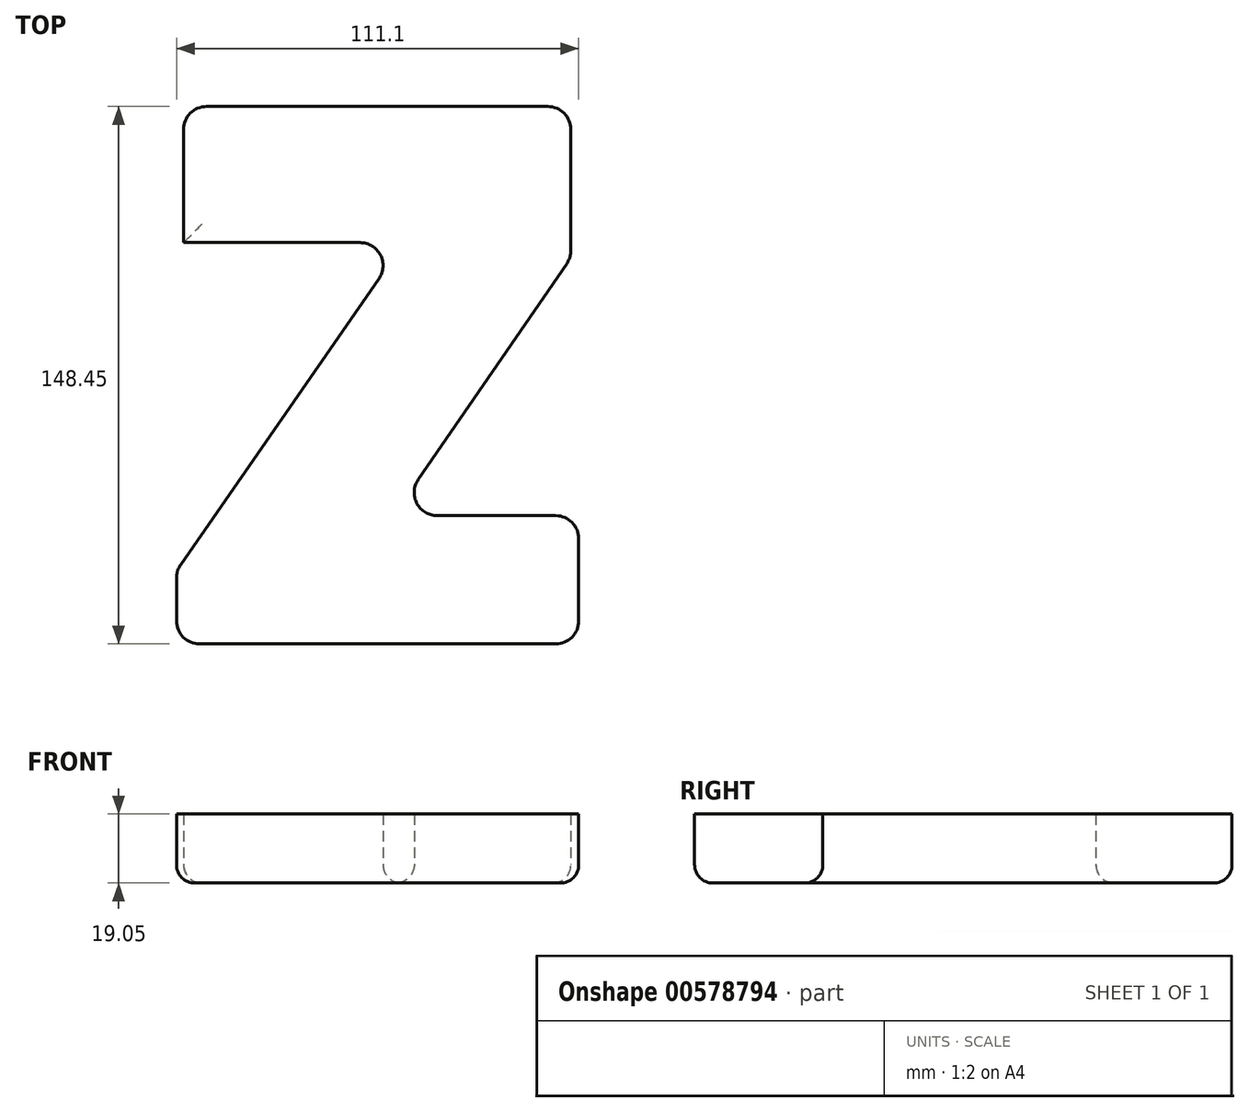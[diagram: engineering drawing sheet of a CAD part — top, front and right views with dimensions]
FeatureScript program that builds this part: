
annotation { "Feature Type Name" : "Feature", "Feature Type Description" : "" }
export const myFeature = defineFeature(function(context is Context, id is Id, definition is map)
    precondition{}
    {
        {
            var Q0;
            Q0=qCreatedBy(makeId("Top.planeOp"),FACE);
            var sketch = newSketch(context, id + "F0", { "sketchPlane" : qUnion([Q0])});
            skText(sketch, "E0", { "text": "Z", "fontName": "OpenSans-Bold.ttf"});
            skLineSegment(sketch, "E1", {"start": v(-54.55, 77.63) * mm, "end": v(-54.55, 38.1) * mm});
            skLineSegment(sketch, "E2", {"start": v(-54.55, 38.1) * mm, "end": v(-5.8, 38.1) * mm});
            skLineSegment(sketch, "E3", {"start": v(-0.58, 28.14) * mm, "end": v(-55.35, -50.87) * mm});
            skLineSegment(sketch, "E4", {"start": v(-56.48, -54.49) * mm, "end": v(-56.48, -66.4) * mm});
            skLineSegment(sketch, "E5", {"start": v(-50.13, -72.75) * mm, "end": v(48.27, -72.75) * mm});
            skLineSegment(sketch, "E6", {"start": v(54.62, -66.4) * mm, "end": v(54.62, -43.67) * mm});
            skLineSegment(sketch, "E7", {"start": v(48.27, -37.32) * mm, "end": v(15.52, -37.32) * mm});
            skLineSegment(sketch, "E8", {"start": v(10.29, -27.38) * mm, "end": v(51.33, 32.37) * mm});
            skLineSegment(sketch, "E9", {"start": v(52.45, 35.97) * mm, "end": v(52.45, 69.35) * mm});
            skLineSegment(sketch, "E10", {"start": v(46.1, 75.7) * mm, "end": v(-48.2, 75.7) * mm});
            skLineSegment(sketch, "E11", {"start": v(-54.55, 69.35) * mm, "end": v(-54.55, 38.1) * mm});
            skPoint(sketch, "E12.visualSharp", {"position": v(-54.55, 75.7) * mm});
            skArc(sketch, "E12.filletArc", {"start": v(-48.2, 75.7) * mm, "mid": v(-52.7, 73.84) * mm, "end": v(-54.55, 69.35) * mm});
            skPoint(sketch, "E13.visualSharp", {"position": v(6.33, 38.1) * mm});
            skArc(sketch, "E13.filletArc", {"start": v(-0.58, 28.14) * mm, "mid": v(-0.17, 34.7) * mm, "end": v(-5.8, 38.1) * mm});
            skPoint(sketch, "E14.visualSharp", {"position": v(-56.48, -52.5) * mm});
            skArc(sketch, "E14.filletArc", {"start": v(-55.35, -50.87) * mm, "mid": v(-56.2, -52.6) * mm, "end": v(-56.48, -54.49) * mm});
            skPoint(sketch, "E15.visualSharp", {"position": v(-56.48, -72.75) * mm});
            skArc(sketch, "E15.filletArc", {"start": v(-56.48, -66.4) * mm, "mid": v(-54.62, -70.89) * mm, "end": v(-50.13, -72.75) * mm});
            skPoint(sketch, "E16.visualSharp", {"position": v(54.62, -72.75) * mm});
            skArc(sketch, "E16.filletArc", {"start": v(48.27, -72.75) * mm, "mid": v(52.76, -70.89) * mm, "end": v(54.62, -66.4) * mm});
            skPoint(sketch, "E17.visualSharp", {"position": v(54.62, -37.32) * mm});
            skArc(sketch, "E17.filletArc", {"start": v(54.62, -43.67) * mm, "mid": v(52.76, -39.18) * mm, "end": v(48.27, -37.32) * mm});
            skPoint(sketch, "E18.visualSharp", {"position": v(3.46, -37.32) * mm});
            skArc(sketch, "E18.filletArc", {"start": v(10.29, -27.38) * mm, "mid": v(9.9, -33.93) * mm, "end": v(15.52, -37.32) * mm});
            skPoint(sketch, "E19.visualSharp", {"position": v(52.45, 34) * mm});
            skArc(sketch, "E19.filletArc", {"start": v(51.33, 32.37) * mm, "mid": v(52.16, 34.09) * mm, "end": v(52.45, 35.97) * mm});
            skPoint(sketch, "E20.visualSharp", {"position": v(52.45, 75.7) * mm});
            skArc(sketch, "E20.filletArc", {"start": v(52.45, 69.35) * mm, "mid": v(50.59, 73.84) * mm, "end": v(46.1, 75.7) * mm});
            skLineSegment(sketch, "E21", {"start": v(-54.55, 75.7) * mm, "end": v(-54.55, 38.1) * mm});
            const initialGuessF0  = {"E0": [-0.06154, -0.07275, 1, 0, 0.15038]};
            skSetInitialGuess(sketch, initialGuessF0);
            skSolve(sketch);
        }
        {
            var Q0;
            {var subQ5=sQuery(id+"F0.wireOp",EDGE,"E2");Q0=makeQuery(id+"F0.imprint","IMPRINT",FACE,{"disambiguationData":[TD([[makeQuery(id+"F0.imprint","IMPRINT",EDGE,{"derivedFrom":subQ5}),1.0]])]});}
            var Q1;
            {var subQ6=sQuery(id+"F0.wireOp",EDGE,"E0.sketch_text.stroke-8");Q1=makeQuery(id+"F0.imprint","IMPRINT",FACE,{"disambiguationData":[TD([[makeQuery(id+"F0.imprint","IMPRINT",EDGE,{"derivedFrom":subQ6}),-1.0]])]});}
            var Q2;
            {var subQ0=sQuery(id+"F0.wireOp",EDGE,"E0.sketch_text.stroke-8");Q2=makeQuery(id+"F0.imprint","IMPRINT",FACE,{"disambiguationData":[TD([[makeQuery(id+"F0.imprint","IMPRINT",EDGE,{"derivedFrom":subQ0}),1.0]])]});}
            extrude(context, id + "F1", {"entities" : qUnion([Q0, Q1, Q2]), "depth" : 19.05 * mm, "offsetDistance" : 25.4 * mm});
        }
        {
            var Q0;
            Q0=makeQuery(id+"F1.opExtrude","CAP_FACE",FACE,{"disambiguationData":[OSD([sQuery(id+"F0.wireOp",EDGE,"E2"),sQuery(id+"F0.wireOp",EDGE,"E3"),sQuery(id+"F0.wireOp",EDGE,"E4"),sQuery(id+"F0.wireOp",EDGE,"E5"),sQuery(id+"F0.wireOp",EDGE,"E6"),sQuery(id+"F0.wireOp",EDGE,"E7"),sQuery(id+"F0.wireOp",EDGE,"E8"),sQuery(id+"F0.wireOp",EDGE,"E9"),sQuery(id+"F0.wireOp",EDGE,"E10"),sQuery(id+"F0.wireOp",EDGE,"E12.filletArc"),sQuery(id+"F0.wireOp",EDGE,"E13.filletArc"),sQuery(id+"F0.wireOp",EDGE,"E14.filletArc"),sQuery(id+"F0.wireOp",EDGE,"E15.filletArc"),sQuery(id+"F0.wireOp",EDGE,"E16.filletArc"),sQuery(id+"F0.wireOp",EDGE,"E17.filletArc"),sQuery(id+"F0.wireOp",EDGE,"E18.filletArc"),sQuery(id+"F0.wireOp",EDGE,"E19.filletArc"),sQuery(id+"F0.wireOp",EDGE,"E20.filletArc"),sQuery(id+"F0.wireOp",EDGE,"E21")])],"isStart":true});
            fillet(context, id + "F2", {"entities" : qUnion([Q0]), "radius" : 5.08 * mm, "tangentPropagation" : true, "allowEdgeOverflow" : false});
        }
    });
